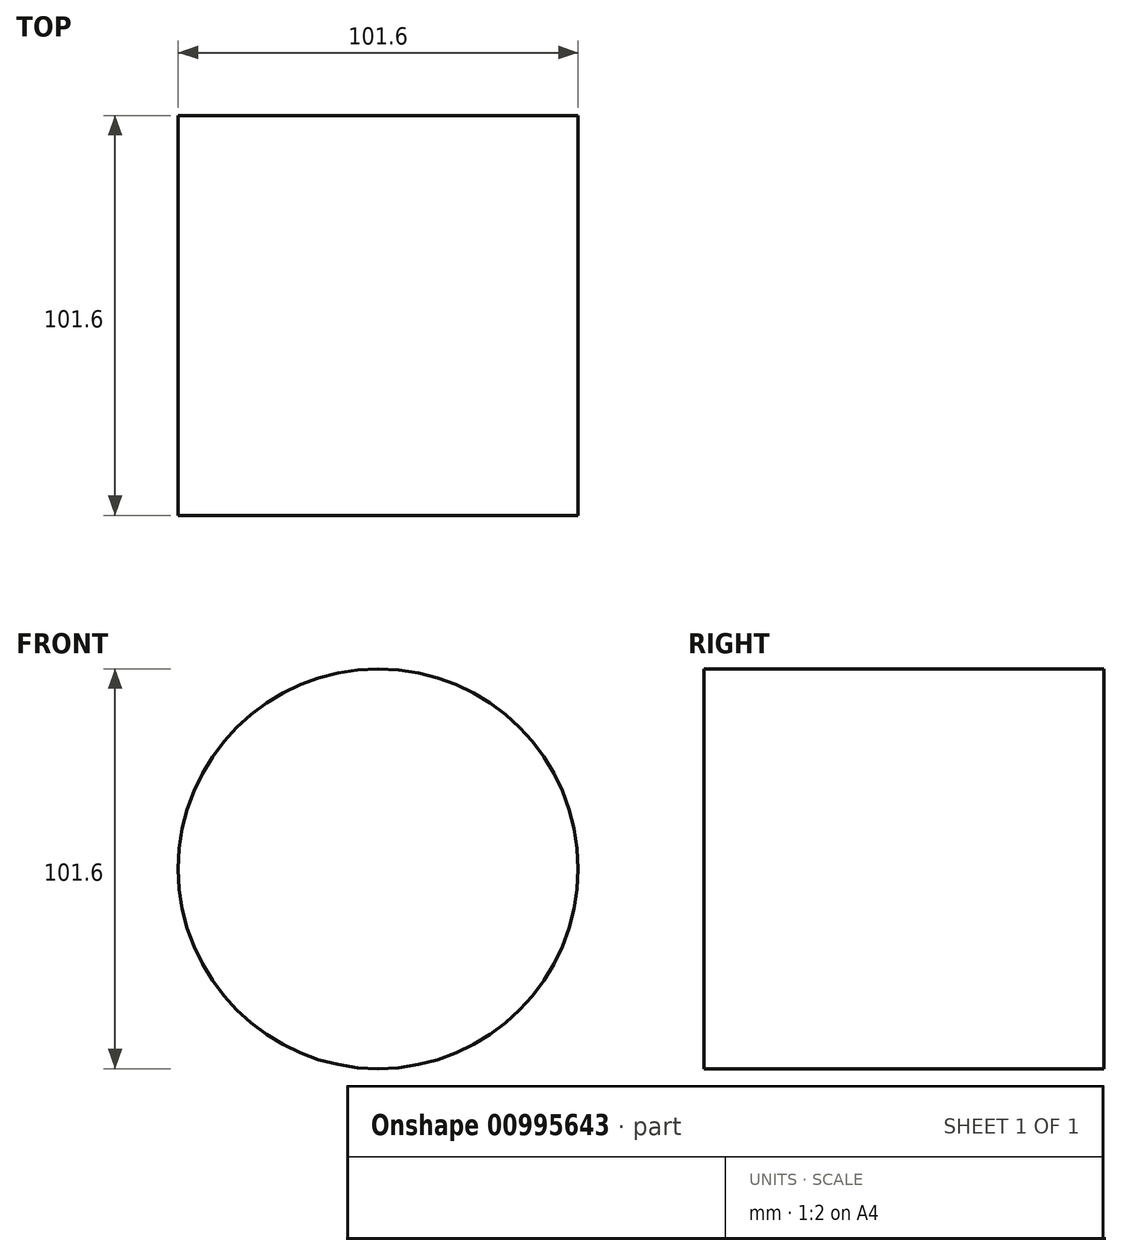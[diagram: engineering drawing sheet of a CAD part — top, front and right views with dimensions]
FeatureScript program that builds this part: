
annotation { "Feature Type Name" : "Feature", "Feature Type Description" : "" }
export const myFeature = defineFeature(function(context is Context, id is Id, definition is map)
    precondition{}
    {
        {
            var Q0;
            Q0=qCreatedBy(makeId("Front.planeOp"),FACE);
            var sketch = newSketch(context, id + "F0", { "sketchPlane" : qUnion([Q0])});
            skCircle(sketch, "E0", {"center": v(0, 0) * mm, "radius": 50.8 * mm});
            skSolve(sketch);
        }
        {
            var Q0;
            Q0 = qSketchRegion(id + "F0", true);
            extrude(context, id + "F1", {"entities" : qUnion([Q0]), "depth" : 101.6 * mm, "offsetDistance" : 25.4 * mm});
        }
    });
